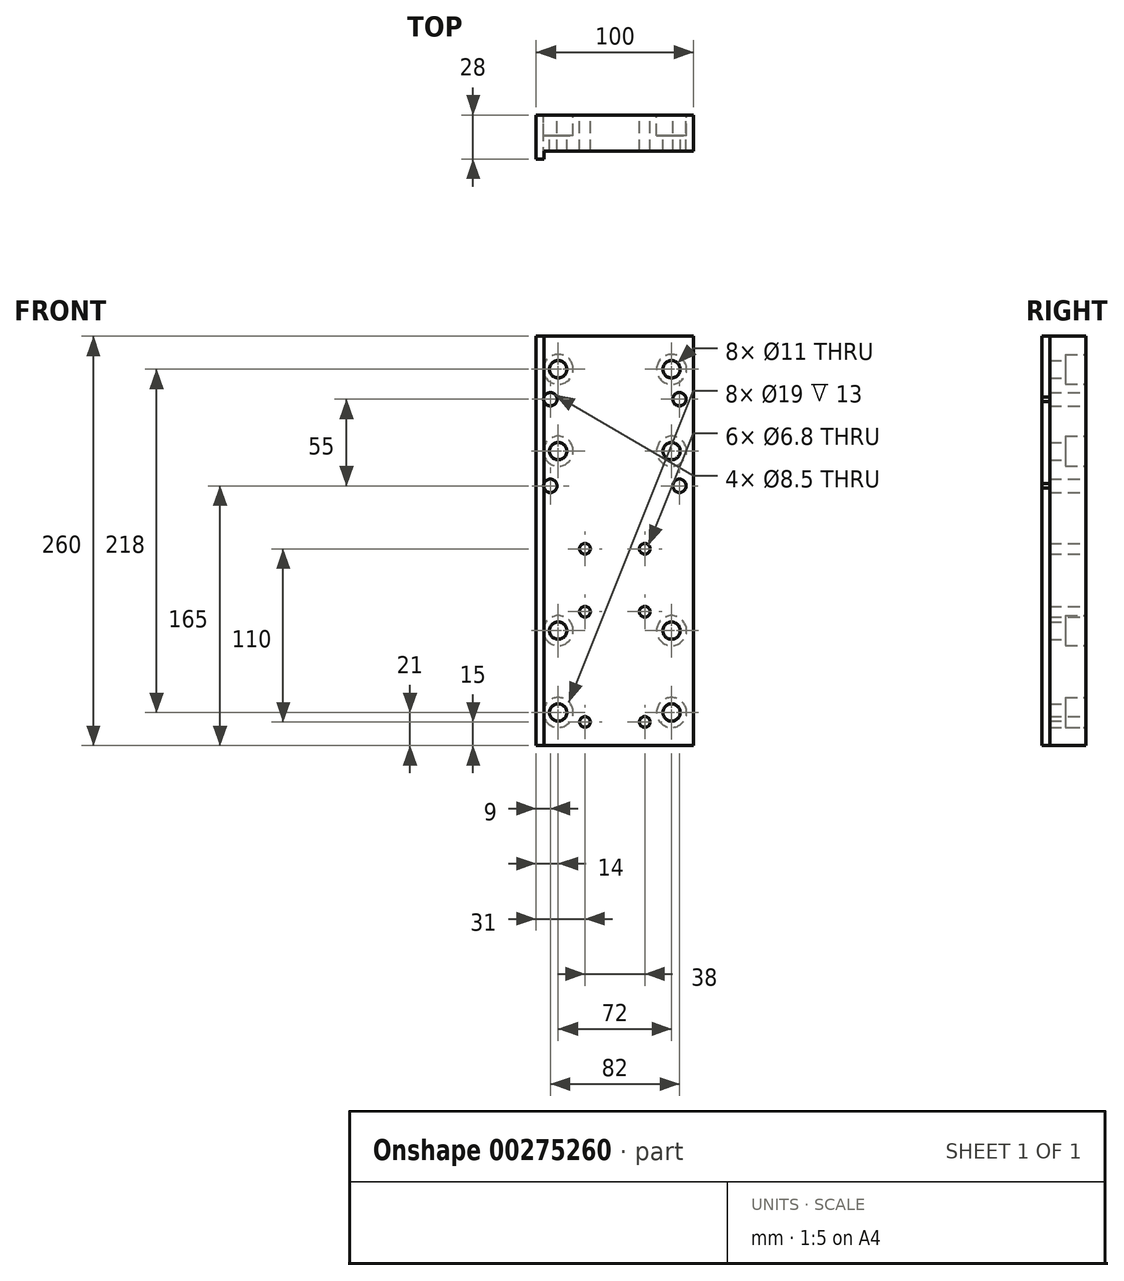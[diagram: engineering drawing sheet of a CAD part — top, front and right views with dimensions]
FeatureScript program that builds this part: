
annotation { "Feature Type Name" : "Feature", "Feature Type Description" : "" }
export const myFeature = defineFeature(function(context is Context, id is Id, definition is map)
    precondition{}
    {
        {
            var Q0;
            Q0=qCreatedBy(makeId("Front.planeOp"),FACE);
            var sketch = newSketch(context, id + "F0", { "sketchPlane" : qUnion([Q0])});
            skLineSegment(sketch, "E0.bottom", {"start": v(50, 130) * mm, "end": v(-50, 130) * mm});
            skLineSegment(sketch, "E0.top", {"start": v(50, -130) * mm, "end": v(-50, -130) * mm});
            skLineSegment(sketch, "E0.left", {"start": v(50, 130) * mm, "end": v(50, -130) * mm});
            skLineSegment(sketch, "E0.right", {"start": v(-50, 130) * mm, "end": v(-50, -130) * mm});
            skPoint(sketch, "E0.middle", {"position": v(0, 0) * mm});
            skLineSegment(sketch, "E1", {"start": v(0, 186.28) * mm, "end": v(0, -202.21) * mm, "construction": true});
            skLineSegment(sketch, "E2", {"start": v(-36, 152.76) * mm, "end": v(-36, -191.83) * mm, "construction": true});
            skLineSegment(sketch, "E3", {"start": v(36, 152.76) * mm, "end": v(36, -190.18) * mm, "construction": true});
            skLineSegment(sketch, "E4", {"start": v(-97.72, 109) * mm, "end": v(110.2, 109) * mm, "construction": true});
            skLineSegment(sketch, "E5", {"start": v(-105.17, 57) * mm, "end": v(111.85, 57) * mm, "construction": true});
            skLineSegment(sketch, "E6", {"start": v(-85.3, -57) * mm, "end": v(85.35, -57) * mm, "construction": true});
            skLineSegment(sketch, "E7", {"start": v(-87.83, -109) * mm, "end": v(103.63, -109) * mm, "construction": true});
            skPoint(sketch, "E8", {"position": v(36, -109) * mm});
            skPoint(sketch, "E9", {"position": v(-36, -109) * mm});
            skPoint(sketch, "E10", {"position": v(-36, -57) * mm});
            skPoint(sketch, "E11", {"position": v(36, -57) * mm});
            skPoint(sketch, "E12", {"position": v(36, 57) * mm});
            skPoint(sketch, "E13", {"position": v(-36, 57) * mm});
            skPoint(sketch, "E14", {"position": v(-36, 109) * mm});
            skPoint(sketch, "E15", {"position": v(36, 109) * mm});
            skLineSegment(sketch, "E16", {"start": v(66.34, -115) * mm, "end": v(-76.85, -115) * mm, "construction": true});
            skLineSegment(sketch, "E17", {"start": v(61.91, -45) * mm, "end": v(-70.22, -45) * mm, "construction": true});
            skLineSegment(sketch, "E18", {"start": v(64.68, 35) * mm, "end": v(-74.09, 35) * mm, "construction": true});
            skLineSegment(sketch, "E19", {"start": v(69.65, -5) * mm, "end": v(-80.72, -5) * mm, "construction": true});
            skLineSegment(sketch, "E20", {"start": v(63.02, 90) * mm, "end": v(-69.67, 90) * mm, "construction": true});
            skPoint(sketch, "E21", {"position": v(19, -115) * mm});
            skPoint(sketch, "E22", {"position": v(-19, -115) * mm});
            skPoint(sketch, "E23", {"position": v(19, -45) * mm});
            skPoint(sketch, "E24", {"position": v(-19, -45) * mm});
            skPoint(sketch, "E25", {"position": v(19, -5) * mm});
            skPoint(sketch, "E26", {"position": v(-19, -5) * mm});
            skPoint(sketch, "E27", {"position": v(41, 35) * mm});
            skPoint(sketch, "E28", {"position": v(-41, 35) * mm});
            skPoint(sketch, "E29", {"position": v(41, 90) * mm});
            skPoint(sketch, "E30", {"position": v(-41, 90) * mm});
            skLineSegment(sketch, "E31", {"start": v(-45, -130) * mm, "end": v(-45, 130) * mm});
            skLineSegment(sketch, "E32", {"start": v(-80, 157.79) * mm, "end": v(-80, -174.8) * mm, "construction": true});
            skSolve(sketch);
        }
        {
            var Q0;
            {var subQ0=sQuery(id+"F0.wireOp",EDGE,"E0.right");Q0=makeQuery(id+"F0.imprint","IMPRINT",FACE,{"disambiguationData":[TD([[makeQuery(id+"F0.imprint","IMPRINT",EDGE,{"derivedFrom":subQ0}),1.0]])]});}
            var Q1;
            {var subQ0=sQuery(id+"F0.wireOp",EDGE,"128ad9ec-08f8-46f6-a475-e2edd0445f690.MirrorCS");Q1=makeQuery(id+"F0.imprint","IMPRINT",FACE,{"disambiguationData":[TD([[makeQuery(id+"F0.imprint","IMPRINT",EDGE,{"derivedFrom":subQ0}),-1.0]])]});}
            extrude(context, id + "F1", {"entities" : qUnion([Q0, Q1]), "depth" : 28 * mm});
        }
        {
            var Q0;
            {var subQ0=sQuery(id+"F0.wireOp",EDGE,"E0.left");Q0=makeQuery(id+"F0.imprint","IMPRINT",FACE,{"disambiguationData":[TD([[makeQuery(id+"F0.imprint","IMPRINT",EDGE,{"derivedFrom":subQ0}),-1.0]])]});}
            var Q1;
            {var subQ0=sQuery(id+"F0.wireOp",EDGE,"a6040214-ca35-4071-b805-a1a1cd6029d30.MirrorCS");Q1=makeQuery(id+"F0.imprint","IMPRINT",FACE,{"disambiguationData":[TD([[makeQuery(id+"F0.imprint","IMPRINT",EDGE,{"derivedFrom":subQ0}),1.0]])]});}
            extrude(context, id + "F2", {"entities" : qUnion([Q0, Q1]), "operationType" : NewBodyOperationType.ADD, "depth" : 23 * mm});
        }
        {
            var Q0;
            Q0=sQuery(id+"F0.wireOp",VERTEX,"E29");
            var Q1;
            Q1=sQuery(id+"F0.wireOp",VERTEX,"E30");
            var Q2;
            Q2=sQuery(id+"F0.wireOp",VERTEX,"E27");
            var Q3;
            Q3=sQuery(id+"F0.wireOp",VERTEX,"E28");
            var Q4;
            Q4=sQuery(id+"F0.wireOp",VERTEX,"108ac730-6808-4052-8798-2e7cf6950e1d0.MirrorP");
            var Q5;
            Q5=sQuery(id+"F0.wireOp",VERTEX,"e780d332-b1ac-4a4a-8ac9-43a6a8f922740.MirrorP");
            var Q6;
            Q6=sQuery(id+"F0.wireOp",VERTEX,"2fa7f7ba-c06d-4768-abbe-afb8684577830.MirrorP");
            var Q7;
            Q7=makeQuery(id+"F1.opExtrude","SWEPT_BODY",BODY,{"disambiguationData":[OSD([sQuery(id+"F0.wireOp",EDGE,"E0.bottom"),sQuery(id+"F0.wireOp",EDGE,"E0.top"),sQuery(id+"F0.wireOp",EDGE,"E0.right"),sQuery(id+"F0.wireOp",EDGE,"E31")])]});
            hole(context, id + "F3", {"style" : HoleStyle.SIMPLE, "endStyle" : HoleEndStyle.THROUGH, "oppositeDirection" : true, "standardTappedOrClearance" : lookupTablePath({ "standard" : "ISO", "engagement" : "75%", "pitch" : "1.5 mm", "size" : "M10", "type" : "Tapped" }), "standardBlindInLast" : lookupTablePath({ "standard" : "ISO", "engagement" : "75%", "pitch" : "1.5 mm", "size" : "M10", "type" : "Tapped" }), "holeDiameter" : 8.5 * mm, "showTappedDepth" : true, "tappedDepth" : 12 * mm, "tapClearance" : 3, "startFromSketch" : true, "locations" : qUnion([Q0, Q1, Q2, Q3, Q4, Q5, Q6]), "scope" : qUnion([Q7]), "majorDiameter" : 10 * mm});
        }
        {
            var Q0;
            Q0=sQuery(id+"F0.wireOp",VERTEX,"E25");
            var Q1;
            Q1=sQuery(id+"F0.wireOp",VERTEX,"E26");
            var Q2;
            Q2=sQuery(id+"F0.wireOp",VERTEX,"E23");
            var Q3;
            Q3=sQuery(id+"F0.wireOp",VERTEX,"E24");
            var Q4;
            Q4=sQuery(id+"F0.wireOp",VERTEX,"E21");
            var Q5;
            Q5=sQuery(id+"F0.wireOp",VERTEX,"E22");
            var Q6;
            Q6=makeQuery(id+"F1.opExtrude","SWEPT_BODY",BODY,{"disambiguationData":[OSD([sQuery(id+"F0.wireOp",EDGE,"E0.bottom"),sQuery(id+"F0.wireOp",EDGE,"E0.top"),sQuery(id+"F0.wireOp",EDGE,"E0.right"),sQuery(id+"F0.wireOp",EDGE,"E31")])]});
            hole(context, id + "F4", {"style" : HoleStyle.SIMPLE, "endStyle" : HoleEndStyle.THROUGH, "oppositeDirection" : true, "standardTappedOrClearance" : lookupTablePath({ "standard" : "ISO", "engagement" : "75%", "pitch" : "1.25 mm", "size" : "M8", "type" : "Tapped" }), "standardBlindInLast" : lookupTablePath({ "standard" : "ISO", "engagement" : "75%", "pitch" : "1.25 mm", "size" : "M8", "type" : "Tapped" }), "holeDiameter" : 6.8 * mm, "showTappedDepth" : true, "tappedDepth" : 19.25 * mm, "tapClearance" : 3, "startFromSketch" : true, "locations" : qUnion([Q0, Q1, Q2, Q3, Q4, Q5]), "scope" : qUnion([Q6]), "majorDiameter" : 8 * mm});
        }
        {
            var Q0;
            Q0=sQuery(id+"F0.wireOp",VERTEX,"E15");
            var Q1;
            Q1=sQuery(id+"F0.wireOp",VERTEX,"E14");
            var Q2;
            Q2=sQuery(id+"F0.wireOp",VERTEX,"E12");
            var Q3;
            Q3=sQuery(id+"F0.wireOp",VERTEX,"E13");
            var Q4;
            Q4=sQuery(id+"F0.wireOp",VERTEX,"E11");
            var Q5;
            Q5=sQuery(id+"F0.wireOp",VERTEX,"E10");
            var Q6;
            Q6=sQuery(id+"F0.wireOp",VERTEX,"E9");
            var Q7;
            Q7=sQuery(id+"F0.wireOp",VERTEX,"E8");
            var Q8;
            Q8=makeQuery(id+"F1.opExtrude","SWEPT_BODY",BODY,{"disambiguationData":[OSD([sQuery(id+"F0.wireOp",EDGE,"E0.bottom"),sQuery(id+"F0.wireOp",EDGE,"E0.top"),sQuery(id+"F0.wireOp",EDGE,"E0.right"),sQuery(id+"F0.wireOp",EDGE,"E31")])]});
            hole(context, id + "F5", {"style" : HoleStyle.C_BORE, "endStyle" : HoleEndStyle.THROUGH, "oppositeDirection" : true, "holeDiameter" : 11 * mm, "cBoreDiameter" : 19 * mm, "cBoreDepth" : 13 * mm, "tappedDepth" : 19.25 * mm, "tapClearance" : 3, "startFromSketch" : true, "locations" : qUnion([Q0, Q1, Q2, Q3, Q4, Q5, Q6, Q7]), "scope" : qUnion([Q8])});
        }
    });
